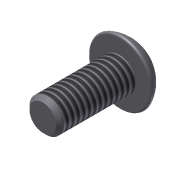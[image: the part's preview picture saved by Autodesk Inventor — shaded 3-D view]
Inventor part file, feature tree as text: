
AUTODESK INVENTOR PART (.ipt)
format: ipt  version: 2011 SP1 (Build 150282100, 282)  size: 127,488 bytes
history: native  units: in
note: dims shown in document units (in); Inventor stores cm internally (conversion verified against a paired STEP export)
features: sketch x3, extrude x2, revolve x1, chamfer x1, thread x1
ambient origin geometry x8: Origin, YZ Plane, XZ Plane, XY Plane, X Axis, Y Axis, Z Axis, Center Point
bodies: Solid1 (feature_tree)
feature tree (8):
  extrude  "Extrusion1"  Depth=0.4375in TaperAngle=0.0deg
  revolve  "Revolution1"  [1 undecoded]
  extrude  "Extrusion2"  Depth=0.125in
  chamfer  "Chamfer1"  Distance=0.0625in
  thread  "Thread1"  [1 undecoded]
  sketch  "Sketch1"  dims[d0=0.19in d1=0.4375in d2=0.0in]
  sketch  "Sketch2"  dims[d3=0.101in d6=0.08in]
  sketch  "Sketch3"  dims[d7=90.0deg d8=0.125in d9=0.0625in d10=0.0in d12=0.1805in d13=0.02in d14=0.125in d15=45.0deg d16=1.0in d17=0.0in]
note: 2 required parameter values undecoded (feature->parameter linkage not recoverable at this tier; creation-order binding heuristic only, values carry confidence <= 0.55)